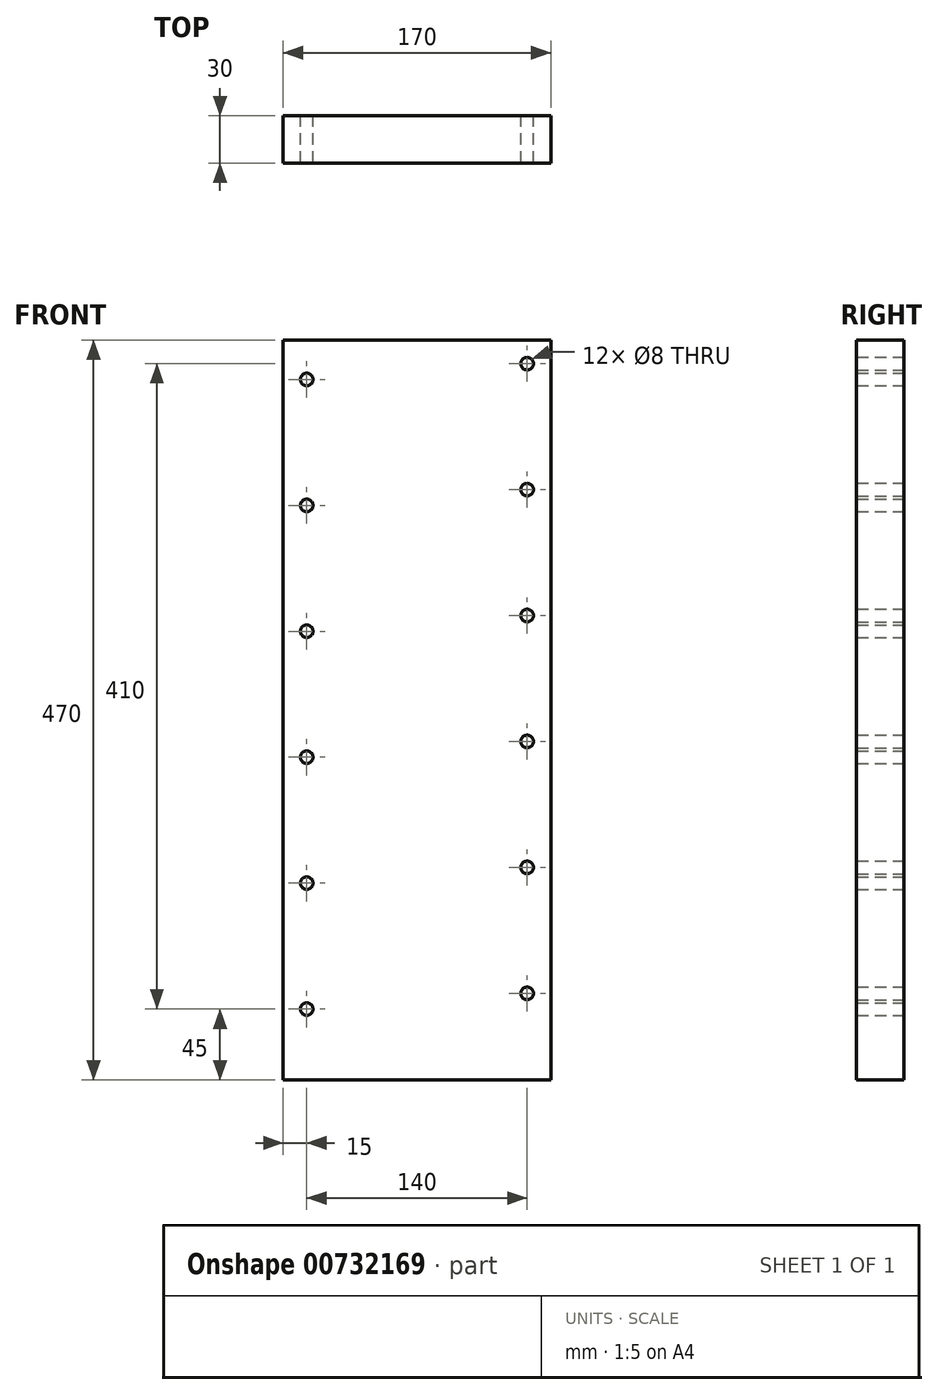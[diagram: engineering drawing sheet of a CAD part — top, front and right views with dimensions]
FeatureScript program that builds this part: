
annotation { "Feature Type Name" : "Feature", "Feature Type Description" : "" }
export const myFeature = defineFeature(function(context is Context, id is Id, definition is map)
    precondition{}
    {
        {
            var Q0;
            Q0=qCreatedBy(makeId("Front.planeOp"),FACE);
            var sketch = newSketch(context, id + "F0", { "sketchPlane" : qUnion([Q0])});
            skLineSegment(sketch, "E0.bottom", {"start": v(0, 0) * mm, "end": v(170, 0) * mm});
            skLineSegment(sketch, "E0.top", {"start": v(0, 470) * mm, "end": v(170, 470) * mm});
            skLineSegment(sketch, "E0.left", {"start": v(0, 0) * mm, "end": v(0, 470) * mm});
            skLineSegment(sketch, "E0.right", {"start": v(170, 0) * mm, "end": v(170, 470) * mm});
            skCircle(sketch, "E1", {"center": v(155, 455) * mm, "radius": 4 * mm});
            skCircle(sketch, "E2.0.1.0", {"center": v(155, 375) * mm, "radius": 4 * mm});
            skCircle(sketch, "E2.0.2.0", {"center": v(155, 295) * mm, "radius": 4 * mm});
            skCircle(sketch, "E2.0.3.0", {"center": v(155, 215) * mm, "radius": 4 * mm});
            skCircle(sketch, "E2.0.4.0", {"center": v(155, 135) * mm, "radius": 4 * mm});
            skCircle(sketch, "E2.0.5.0", {"center": v(155, 55) * mm, "radius": 4 * mm});
            skLineSegment(sketch, "E2.direction1", {"start": v(155, 455) * mm, "end": v(180, 455) * mm, "construction": true});
            skLineSegment(sketch, "E2.direction2", {"start": v(155, 455) * mm, "end": v(155, 375) * mm, "construction": true});
            skCircle(sketch, "E3", {"center": v(15, 445) * mm, "radius": 4 * mm});
            skCircle(sketch, "E4.0.1.0", {"center": v(15, 365) * mm, "radius": 4 * mm});
            skCircle(sketch, "E4.0.2.0", {"center": v(15, 285) * mm, "radius": 4 * mm});
            skCircle(sketch, "E4.0.3.0", {"center": v(15, 205) * mm, "radius": 4 * mm});
            skCircle(sketch, "E4.0.4.0", {"center": v(15, 125) * mm, "radius": 4 * mm});
            skCircle(sketch, "E4.0.5.0", {"center": v(15, 45) * mm, "radius": 4 * mm});
            skLineSegment(sketch, "E4.direction1", {"start": v(15, 445) * mm, "end": v(40, 445) * mm, "construction": true});
            skLineSegment(sketch, "E4.direction2", {"start": v(15, 445) * mm, "end": v(15, 365) * mm, "construction": true});
            skSolve(sketch);
        }
        {
            var Q0;
            Q0=makeQuery(id+"F0.imprint","IMPRINT",FACE,{"disambiguationData":[TD([[makeQuery(id+"F0.imprint","IMPRINT",EDGE,{"derivedFrom":sQuery(id+"F0.wireOp",EDGE,"E0.bottom")}),1.0]])]});
            extrude(context, id + "F1", {"entities" : qUnion([Q0]), "depth" : 30 * mm, "offsetDistance" : 25 * mm});
        }
    });
